# Revit family: Haworth_Tibas_Desk_BenchWorkstation_EU_PRELIMINARY
name_source: partatom
category: Furniture
units: mm (PartAtom-declared; Revit-internal decimal feet)

## family parameters
Always vertical = Yes
Cut with Voids When Loaded = No
OmniClass Number = 23.40.70.14.64.11
OmniClass Title = Office Furniture
Room Calculation Point = No
Shared = No
Work Plane-Based = No

## types (2) — shared parameters
Actual Depth = 160 cm
Actual Height = 84 cm
Assembly Code = E2020200
Cable Tray Finish = Haworth _ Paint _ Metallic Silver
Description = Haworth - Tibas - Desk - Bench Workstation
Flip Top Cable Outlet = No
Horizontal Cable Tray Wire Double = No
Horizontal Cable Tray Wire Double Small = No
Leg Depth = 120 cm
Leg Height = 80 cm
Manufacturer = Haworth
Model = TIDWXX16
Product URL = https://www.haworth.com
Return Extension = No
Revision Number = 1
Round Cable Outlet = No
Size = Verify Final Dim.w/ Haworth
Structure = Yes
Trim Finish = Haworth _ Polymer _ Undecided
U Shape Cable Outlet = No
URL = https://www.haworth.com
Warranty = http://www.haworth.com
Worksurface Depth = 80 cm

## per-type parameters (varying)
| type | Accessory Kit | Actual Width | Cable Tray Width | Epure Cable Outlet | Horizontal Cable Tray Double | Large | No Accessory Kit | Small | Worksurface Width |
| 320 x 160 | No | 320 cm | 270 cm | No | No | Yes | Yes | No | 160 cm |
| 160 x 160 | Yes | 160 cm | 110 cm | Yes | Yes | No | No | Yes | 80 cm |

## geometry (parser evidence)
native form markers: Sweep x44
no freeform markers — native parametric forms only
